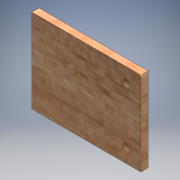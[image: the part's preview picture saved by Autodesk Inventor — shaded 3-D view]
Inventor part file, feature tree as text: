
AUTODESK INVENTOR PART (.ipt)
format: ipt  version: 2016 (Build 200138000, 138)  size: 124,416 bytes
history: native  units: mm
features: sketch x3, extrude x1, hole x1
ambient origin geometry x8: Origin, YZ Plane, XZ Plane, XY Plane, X Axis, Y Axis, Z Axis, Center Point
bodies: Solid1 (feature_tree)
feature tree (5):
  sketch  "Sketch1"  dims[d0=45.5mm d1=35.0mm]
  extrude  "Extrusion1"  Depth=35.0mm
  hole  "Hole1"  [1 undecoded]
  sketch  "Sketch2"  dims[d2=3.0mm d3=0.0mm d4=2.0mm]
  sketch  "Sketch3"  dims[d5=6.0mm d6=6.0mm d7=2.0mm d8=6.0mm d9=6.0mm d10=3.0mm d11=6.0mm d12=4.0mm d13=2.0mm d14=90.0deg d15=8.0mm d16=20.594885mm]
note: 1 required parameter value undecoded (feature->parameter linkage not recoverable at this tier; creation-order binding heuristic only, values carry confidence <= 0.55)
